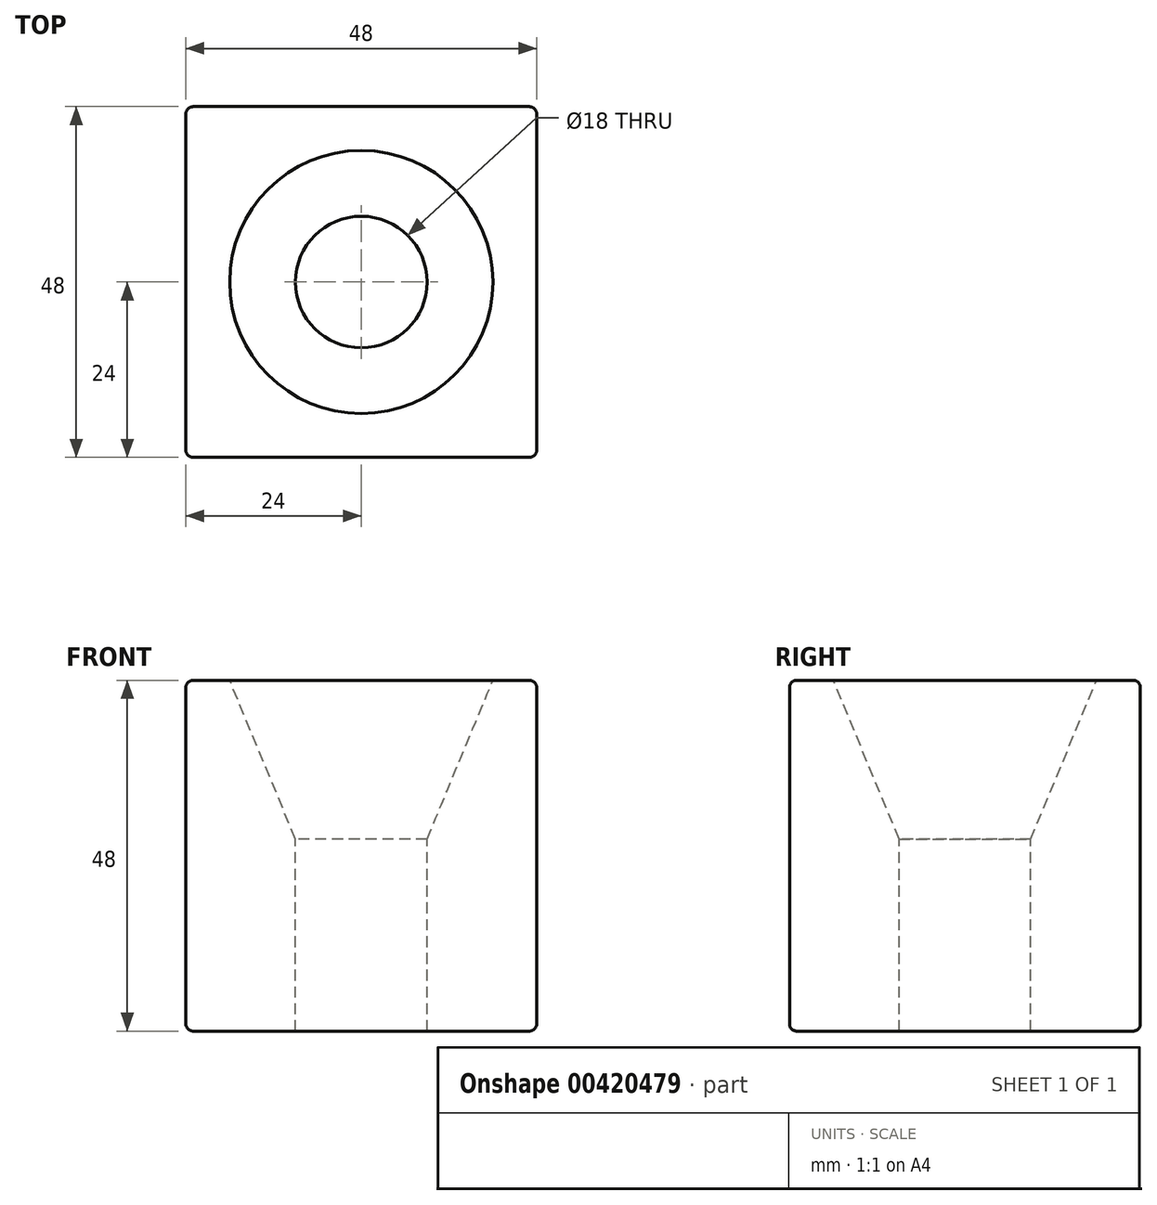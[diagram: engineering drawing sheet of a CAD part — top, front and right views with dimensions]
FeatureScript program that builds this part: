
annotation { "Feature Type Name" : "Feature", "Feature Type Description" : "" }
export const myFeature = defineFeature(function(context is Context, id is Id, definition is map)
    precondition{}
    {
        {
            var Q0;
            Q0=qCreatedBy(makeId("Front.planeOp"),FACE);
            var sketch = newSketch(context, id + "F0", { "sketchPlane" : qUnion([Q0])});
            skLineSegment(sketch, "E0.bottom", {"start": v(-24, 24) * mm, "end": v(24, 24) * mm});
            skLineSegment(sketch, "E0.top", {"start": v(-24, -24) * mm, "end": v(24, -24) * mm});
            skLineSegment(sketch, "E0.left", {"start": v(-24, 24) * mm, "end": v(-24, -24) * mm});
            skLineSegment(sketch, "E0.right", {"start": v(24, 24) * mm, "end": v(24, -24) * mm});
            skPoint(sketch, "E0.middle", {"position": v(0, 0) * mm});
            skSolve(sketch);
        }
        {
            var Q0;
            Q0=makeQuery(id+"F0.imprint","IMPRINT",FACE,{"disambiguationData":[TD([[makeQuery(id+"F0.imprint","IMPRINT",EDGE,{"derivedFrom":sQuery(id+"F0.wireOp",EDGE,"E0.bottom")}),-1.0]])]});
            extrude(context, id + "F1", {"entities" : qUnion([Q0]), "depth" : 48 * mm});
        }
        {
            var Q0;
            Q0=makeQuery(id+"F1.opExtrude","SWEPT_EDGE",EDGE,{"disambiguationData":[OSD([sQuery(id+"F0.wireOp",EDGE,"E0.bottom"),sQuery(id+"F0.wireOp",EDGE,"E0.right")])]});
            fillet(context, id + "F2", {"entities" : qUnion([Q0]), "radius" : 1 * mm, "tangentPropagation" : true, "allowEdgeOverflow" : false});
        }
        {
            var Q0;
            Q0=makeQuery(id+"F1.opExtrude","SWEPT_EDGE",EDGE,{"disambiguationData":[OSD([sQuery(id+"F0.wireOp",EDGE,"E0.bottom"),sQuery(id+"F0.wireOp",EDGE,"E0.left")])]});
            var Q1;
            Q1=makeQuery(id+"F1.opExtrude","CAP_EDGE",EDGE,{"disambiguationData":[OSD([sQuery(id+"F0.wireOp",EDGE,"E0.bottom")])],"isStart":true});
            var Q2;
            Q2=makeQuery(id+"F1.opExtrude","CAP_EDGE",EDGE,{"disambiguationData":[OSD([sQuery(id+"F0.wireOp",EDGE,"E0.bottom")])],"isStart":false});
            fillet(context, id + "F3", {"entities" : qUnion([Q0, Q1, Q2]), "radius" : 1 * mm, "tangentPropagation" : true, "allowEdgeOverflow" : false});
        }
        {
            var Q0;
            Q0=makeQuery(id+"F1.opExtrude","CAP_EDGE",EDGE,{"disambiguationData":[OSD([sQuery(id+"F0.wireOp",EDGE,"E0.left")])],"isStart":false});
            var Q1;
            {var subQ0=sQuery(id+"F0.wireOp",EDGE,"E0.right");Q1=makeQuery(id+"F3.opFillet","BLEND_EDGE",EDGE,{"blendedFrom":[makeQuery(id+"F1.opExtrude","CAP_EDGE",EDGE,{"disambiguationData":[OSD([subQ0])],"isStart":false}),makeQuery(id+"F1.opExtrude","CAP_FACE",FACE,{"disambiguationData":[OSD([sQuery(id+"F0.wireOp",EDGE,"E0.bottom"),sQuery(id+"F0.wireOp",EDGE,"E0.top"),sQuery(id+"F0.wireOp",EDGE,"E0.left"),subQ0])],"isStart":false})],"blendedInto":[makeQuery(id+"F1.opExtrude","CAP_FACE",FACE,{"disambiguationData":[OSD([sQuery(id+"F0.wireOp",EDGE,"E0.bottom"),sQuery(id+"F0.wireOp",EDGE,"E0.top"),sQuery(id+"F0.wireOp",EDGE,"E0.left"),subQ0])],"isStart":false})]});}
            var Q2;
            {var subQ0=sQuery(id+"F0.wireOp",EDGE,"E0.right");Q2=makeQuery(id+"F3.opFillet","BLEND_EDGE",EDGE,{"blendedFrom":[makeQuery(id+"F1.opExtrude","CAP_EDGE",EDGE,{"disambiguationData":[OSD([subQ0])],"isStart":true}),makeQuery(id+"F1.opExtrude","CAP_FACE",FACE,{"disambiguationData":[OSD([sQuery(id+"F0.wireOp",EDGE,"E0.bottom"),sQuery(id+"F0.wireOp",EDGE,"E0.top"),sQuery(id+"F0.wireOp",EDGE,"E0.left"),subQ0])],"isStart":true})],"blendedInto":[makeQuery(id+"F1.opExtrude","CAP_FACE",FACE,{"disambiguationData":[OSD([sQuery(id+"F0.wireOp",EDGE,"E0.bottom"),sQuery(id+"F0.wireOp",EDGE,"E0.top"),sQuery(id+"F0.wireOp",EDGE,"E0.left"),subQ0])],"isStart":true})]});}
            var Q3;
            Q3=makeQuery(id+"F1.opExtrude","CAP_EDGE",EDGE,{"disambiguationData":[OSD([sQuery(id+"F0.wireOp",EDGE,"E0.left")])],"isStart":true});
            var Q4;
            Q4=makeQuery(id+"F1.opExtrude","CAP_EDGE",EDGE,{"disambiguationData":[OSD([sQuery(id+"F0.wireOp",EDGE,"E0.top")])],"isStart":true});
            var Q5;
            Q5=makeQuery(id+"F1.opExtrude","SWEPT_EDGE",EDGE,{"disambiguationData":[OSD([sQuery(id+"F0.wireOp",EDGE,"E0.top"),sQuery(id+"F0.wireOp",EDGE,"E0.left")])]});
            var Q6;
            Q6=makeQuery(id+"F1.opExtrude","CAP_EDGE",EDGE,{"disambiguationData":[OSD([sQuery(id+"F0.wireOp",EDGE,"E0.top")])],"isStart":false});
            var Q7;
            Q7=makeQuery(id+"F1.opExtrude","SWEPT_EDGE",EDGE,{"disambiguationData":[OSD([sQuery(id+"F0.wireOp",EDGE,"E0.top"),sQuery(id+"F0.wireOp",EDGE,"E0.right")])]});
            fillet(context, id + "F4", {"entities" : qUnion([Q0, Q1, Q2, Q3, Q4, Q5, Q6, Q7]), "radius" : 1 * mm, "tangentPropagation" : true, "allowEdgeOverflow" : false});
        }
        {
            var Q0;
            Q0=makeQuery(id+"F1.opExtrude","SWEPT_FACE",FACE,{"disambiguationData":[OSD([sQuery(id+"F0.wireOp",EDGE,"E0.bottom")])]});
            var sketch = newSketch(context, id + "F5", { "sketchPlane" : qUnion([Q0])});
            skPoint(sketch, "E1", {"position": v(0, -24) * mm});
            skPoint(sketch, "E1.positionSnap0", {"position": v(23, -24) * mm});
            skSolve(sketch);
        }
        {
            var Q0;
            Q0=sQuery(id+"F5.wireOp",VERTEX,"E1");
            var Q1;
            Q1=makeQuery(id+"F1.opExtrude","SWEPT_BODY",BODY,{"disambiguationData":[OSD([sQuery(id+"F0.wireOp",EDGE,"E0.bottom"),sQuery(id+"F0.wireOp",EDGE,"E0.top"),sQuery(id+"F0.wireOp",EDGE,"E0.left"),sQuery(id+"F0.wireOp",EDGE,"E0.right")])]});
            hole(context, id + "F6", {"style" : HoleStyle.C_SINK, "endStyle" : HoleEndStyle.THROUGH, "holeDiameter" : 18 * mm, "cSinkDiameter" : 36 * mm, "cSinkAngle" : 45 * degree, "isTappedThrough" : true, "tappedDepth" : 12 * mm, "tapClearance" : 3, "locations" : qUnion([Q0]), "scope" : qUnion([Q1])});
        }
    });
